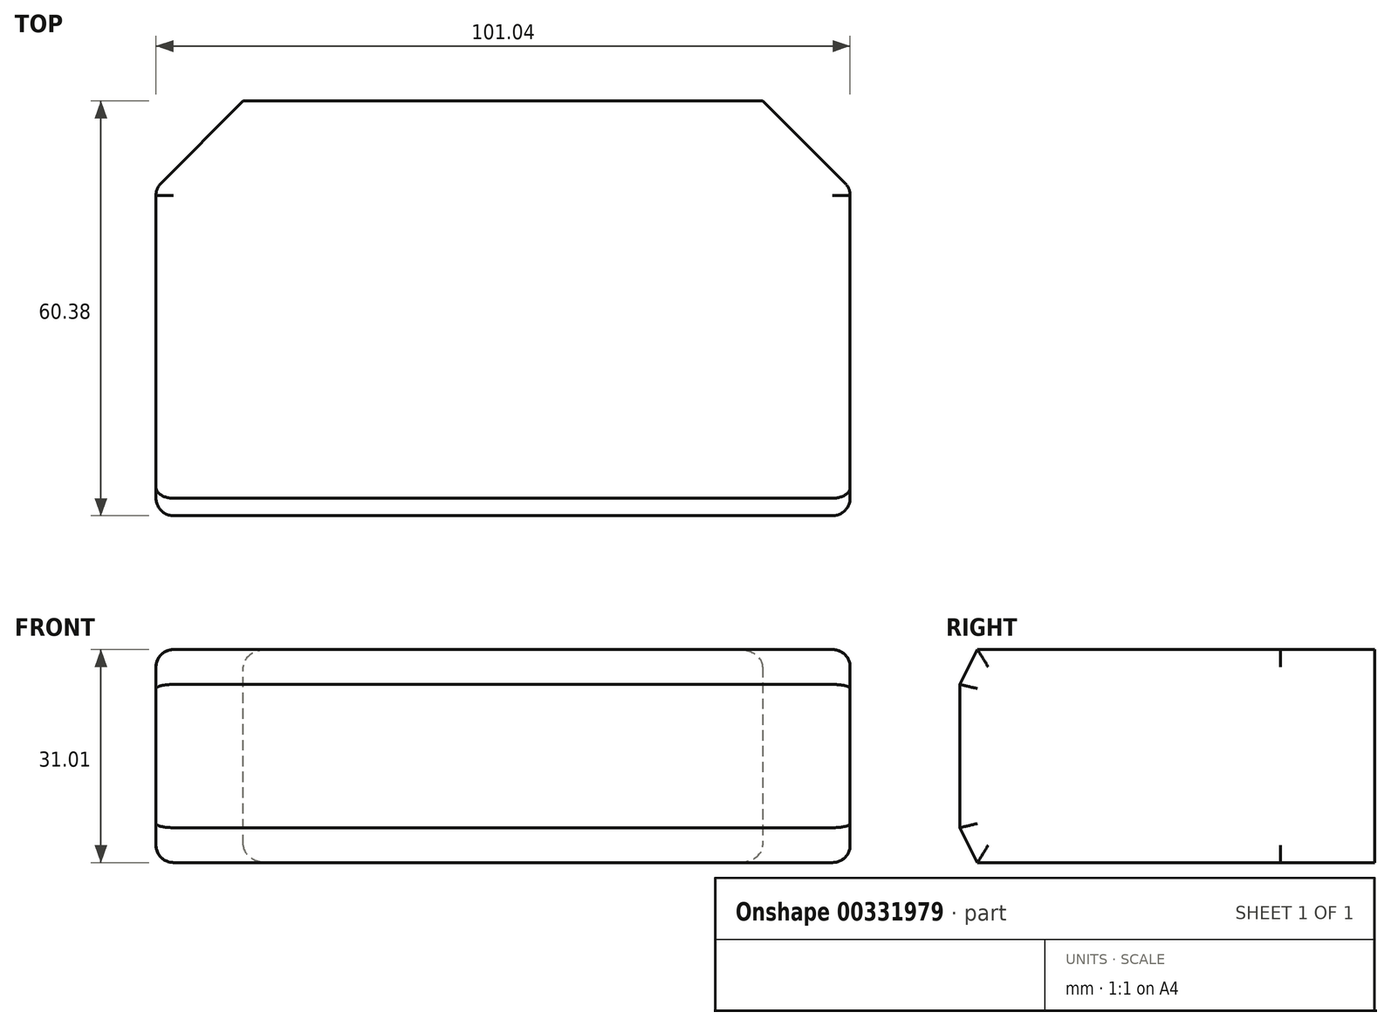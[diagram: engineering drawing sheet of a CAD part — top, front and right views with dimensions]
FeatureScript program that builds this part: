
annotation { "Feature Type Name" : "Feature", "Feature Type Description" : "" }
export const myFeature = defineFeature(function(context is Context, id is Id, definition is map)
    precondition{}
    {
        {
            var Q0;
            Q0=qCreatedBy(makeId("Top.planeOp"),FACE);
            var sketch = newSketch(context, id + "F0", { "sketchPlane" : qUnion([Q0])});
            skLineSegment(sketch, "E0.bottom", {"start": v(50.52, 30.19) * mm, "end": v(-50.52, 30.19) * mm});
            skLineSegment(sketch, "E0.top", {"start": v(50.52, -30.19) * mm, "end": v(-50.52, -30.19) * mm});
            skLineSegment(sketch, "E0.left", {"start": v(50.52, 30.19) * mm, "end": v(50.52, -30.19) * mm});
            skLineSegment(sketch, "E0.right", {"start": v(-50.52, 30.19) * mm, "end": v(-50.52, -30.19) * mm});
            skPoint(sketch, "E0.middle", {"position": v(0, 0) * mm});
            skSolve(sketch);
        }
        {
            var Q0;
            Q0 = qSketchRegion(id + "F0", true);
            extrude(context, id + "F1", {"entities" : qUnion([Q0]), "depth" : 31.01 * mm});
        }
        {
            var Q0;
            Q0=makeQuery(id+"F1.opExtrude","SWEPT_FACE",FACE,{"disambiguationData":[OSD([sQuery(id+"F0.wireOp",EDGE,"E0.top")])]});
            var sketch = newSketch(context, id + "F2", { "sketchPlane" : qUnion([Q0])});
            skSolve(sketch);
        }
        {
            var Q0;
            Q0=makeQuery(id+"F1.opExtrude","CAP_EDGE",EDGE,{"disambiguationData":[OSD([sQuery(id+"F0.wireOp",EDGE,"E0.top")])],"isStart":false});
            var Q1;
            Q1=makeQuery(id+"F1.opExtrude","CAP_EDGE",EDGE,{"disambiguationData":[OSD([sQuery(id+"F0.wireOp",EDGE,"E0.top")])],"isStart":true});
            chamfer(context, id + "F3", {"entities" : qUnion([Q0, Q1]), "chamferType" : ChamferType.TWO_OFFSETS, "width1" : 5.08 * mm, "oppositeDirection" : false, "width2" : 2.54 * mm, "tangentPropagation" : true});
        }
        {
            var Q0;
            Q0=makeQuery(id+"F1.opExtrude","SWEPT_EDGE",EDGE,{"disambiguationData":[OSD([sQuery(id+"F0.wireOp",EDGE,"E0.bottom"),sQuery(id+"F0.wireOp",EDGE,"E0.left")])]});
            var Q1;
            Q1=makeQuery(id+"F1.opExtrude","SWEPT_EDGE",EDGE,{"disambiguationData":[OSD([sQuery(id+"F0.wireOp",EDGE,"E0.bottom"),sQuery(id+"F0.wireOp",EDGE,"E0.right")])]});
            chamfer(context, id + "F4", {"entities" : qUnion([Q0, Q1]), "width" : 12.7 * mm, "tangentPropagation" : true});
        }
        {
            var Q0;
            Q0=makeQuery(id+"F1.opExtrude","SWEPT_EDGE",EDGE,{"disambiguationData":[OSD([sQuery(id+"F0.wireOp",EDGE,"E0.top"),sQuery(id+"F0.wireOp",EDGE,"E0.left")])]});
            var Q1;
            Q1=makeQuery(id+"F3.opChamfer","BLEND_EDGE",EDGE,{"blendedFrom":[makeQuery(id+"F1.opExtrude","CAP_EDGE",EDGE,{"disambiguationData":[OSD([sQuery(id+"F0.wireOp",EDGE,"E0.top")])],"isStart":false}),makeQuery(id+"F1.opExtrude","SWEPT_FACE",FACE,{"disambiguationData":[OSD([sQuery(id+"F0.wireOp",EDGE,"E0.left")])]})],"blendedInto":[makeQuery(id+"F1.opExtrude","SWEPT_FACE",FACE,{"disambiguationData":[OSD([sQuery(id+"F0.wireOp",EDGE,"E0.left")])]})]});
            var Q2;
            Q2=makeQuery(id+"F1.opExtrude","CAP_EDGE",EDGE,{"disambiguationData":[OSD([sQuery(id+"F0.wireOp",EDGE,"E0.left")])],"isStart":false});
            var Q3;
            Q3=makeQuery(id+"F1.opExtrude","CAP_EDGE",EDGE,{"disambiguationData":[OSD([sQuery(id+"F0.wireOp",EDGE,"E0.left")])],"isStart":true});
            var Q4;
            Q4=makeQuery(id+"F3.opChamfer","BLEND_EDGE",EDGE,{"blendedFrom":[makeQuery(id+"F1.opExtrude","CAP_EDGE",EDGE,{"disambiguationData":[OSD([sQuery(id+"F0.wireOp",EDGE,"E0.top")])],"isStart":true}),makeQuery(id+"F1.opExtrude","SWEPT_FACE",FACE,{"disambiguationData":[OSD([sQuery(id+"F0.wireOp",EDGE,"E0.left")])]})],"blendedInto":[makeQuery(id+"F1.opExtrude","SWEPT_FACE",FACE,{"disambiguationData":[OSD([sQuery(id+"F0.wireOp",EDGE,"E0.left")])]})]});
            var Q5;
            Q5=makeQuery(id+"F1.opExtrude","CAP_EDGE",EDGE,{"disambiguationData":[OSD([sQuery(id+"F0.wireOp",EDGE,"E0.right")])],"isStart":false});
            var Q6;
            Q6=makeQuery(id+"F1.opExtrude","SWEPT_EDGE",EDGE,{"disambiguationData":[OSD([sQuery(id+"F0.wireOp",EDGE,"E0.top"),sQuery(id+"F0.wireOp",EDGE,"E0.right")])]});
            var Q7;
            Q7=makeQuery(id+"F3.opChamfer","BLEND_EDGE",EDGE,{"blendedFrom":[makeQuery(id+"F1.opExtrude","CAP_EDGE",EDGE,{"disambiguationData":[OSD([sQuery(id+"F0.wireOp",EDGE,"E0.top")])],"isStart":false}),makeQuery(id+"F1.opExtrude","SWEPT_FACE",FACE,{"disambiguationData":[OSD([sQuery(id+"F0.wireOp",EDGE,"E0.right")])]})],"blendedInto":[makeQuery(id+"F1.opExtrude","SWEPT_FACE",FACE,{"disambiguationData":[OSD([sQuery(id+"F0.wireOp",EDGE,"E0.right")])]})]});
            var Q8;
            Q8=makeQuery(id+"F3.opChamfer","BLEND_EDGE",EDGE,{"blendedFrom":[makeQuery(id+"F1.opExtrude","CAP_EDGE",EDGE,{"disambiguationData":[OSD([sQuery(id+"F0.wireOp",EDGE,"E0.top")])],"isStart":true}),makeQuery(id+"F1.opExtrude","SWEPT_FACE",FACE,{"disambiguationData":[OSD([sQuery(id+"F0.wireOp",EDGE,"E0.right")])]})],"blendedInto":[makeQuery(id+"F1.opExtrude","SWEPT_FACE",FACE,{"disambiguationData":[OSD([sQuery(id+"F0.wireOp",EDGE,"E0.right")])]})]});
            var Q9;
            Q9=makeQuery(id+"F1.opExtrude","CAP_EDGE",EDGE,{"disambiguationData":[OSD([sQuery(id+"F0.wireOp",EDGE,"E0.right")])],"isStart":true});
            fillet(context, id + "F5", {"entities" : qUnion([Q0, Q1, Q2, Q3, Q4, Q5, Q6, Q7, Q8, Q9]), "radius" : 2.54 * mm, "tangentPropagation" : true, "allowEdgeOverflow" : false});
        }
        {
            var Q0;
            {var subQ0=sQuery(id+"F0.wireOp",EDGE,"E0.left");var subQ1=sQuery(id+"F0.wireOp",EDGE,"E0.bottom");Q0=makeQuery(id+"F4.opChamfer","BLEND_EDGE",EDGE,{"blendedFrom":[makeQuery(id+"F1.opExtrude","SWEPT_EDGE",EDGE,{"disambiguationData":[OSD([subQ1,subQ0])]}),makeQuery(id+"F1.opExtrude","CAP_FACE",FACE,{"disambiguationData":[OSD([subQ1,sQuery(id+"F0.wireOp",EDGE,"E0.top"),subQ0,sQuery(id+"F0.wireOp",EDGE,"E0.right")])],"isStart":false})],"blendedInto":[makeQuery(id+"F1.opExtrude","CAP_FACE",FACE,{"disambiguationData":[OSD([subQ1,sQuery(id+"F0.wireOp",EDGE,"E0.top"),subQ0,sQuery(id+"F0.wireOp",EDGE,"E0.right")])],"isStart":false})]});}
            var Q1;
            {var subQ0=sQuery(id+"F0.wireOp",EDGE,"E0.left");var subQ1=sQuery(id+"F0.wireOp",EDGE,"E0.bottom");Q1=makeQuery(id+"F4.opChamfer","BLEND_EDGE",EDGE,{"blendedFrom":[makeQuery(id+"F1.opExtrude","SWEPT_EDGE",EDGE,{"disambiguationData":[OSD([subQ1,subQ0])]}),makeQuery(id+"F1.opExtrude","CAP_FACE",FACE,{"disambiguationData":[OSD([subQ1,sQuery(id+"F0.wireOp",EDGE,"E0.top"),subQ0,sQuery(id+"F0.wireOp",EDGE,"E0.right")])],"isStart":true})],"blendedInto":[makeQuery(id+"F1.opExtrude","CAP_FACE",FACE,{"disambiguationData":[OSD([subQ1,sQuery(id+"F0.wireOp",EDGE,"E0.top"),subQ0,sQuery(id+"F0.wireOp",EDGE,"E0.right")])],"isStart":true})]});}
            var Q2;
            {var subQ0=sQuery(id+"F0.wireOp",EDGE,"E0.right");var subQ1=sQuery(id+"F0.wireOp",EDGE,"E0.bottom");Q2=makeQuery(id+"F4.opChamfer","BLEND_EDGE",EDGE,{"blendedFrom":[makeQuery(id+"F1.opExtrude","SWEPT_EDGE",EDGE,{"disambiguationData":[OSD([subQ1,subQ0])]}),makeQuery(id+"F1.opExtrude","CAP_FACE",FACE,{"disambiguationData":[OSD([subQ1,sQuery(id+"F0.wireOp",EDGE,"E0.top"),sQuery(id+"F0.wireOp",EDGE,"E0.left"),subQ0])],"isStart":false})],"blendedInto":[makeQuery(id+"F1.opExtrude","CAP_FACE",FACE,{"disambiguationData":[OSD([subQ1,sQuery(id+"F0.wireOp",EDGE,"E0.top"),sQuery(id+"F0.wireOp",EDGE,"E0.left"),subQ0])],"isStart":false})]});}
            var Q3;
            {var subQ0=sQuery(id+"F0.wireOp",EDGE,"E0.right");var subQ1=sQuery(id+"F0.wireOp",EDGE,"E0.bottom");Q3=makeQuery(id+"F4.opChamfer","BLEND_EDGE",EDGE,{"blendedFrom":[makeQuery(id+"F1.opExtrude","SWEPT_EDGE",EDGE,{"disambiguationData":[OSD([subQ1,subQ0])]}),makeQuery(id+"F1.opExtrude","CAP_FACE",FACE,{"disambiguationData":[OSD([subQ1,sQuery(id+"F0.wireOp",EDGE,"E0.top"),sQuery(id+"F0.wireOp",EDGE,"E0.left"),subQ0])],"isStart":true})],"blendedInto":[makeQuery(id+"F1.opExtrude","CAP_FACE",FACE,{"disambiguationData":[OSD([subQ1,sQuery(id+"F0.wireOp",EDGE,"E0.top"),sQuery(id+"F0.wireOp",EDGE,"E0.left"),subQ0])],"isStart":true})]});}
            fillet(context, id + "F6", {"entities" : qUnion([Q0, Q1, Q2, Q3]), "radius" : 2.54 * mm, "tangentPropagation" : true, "allowEdgeOverflow" : false});
        }
    });
